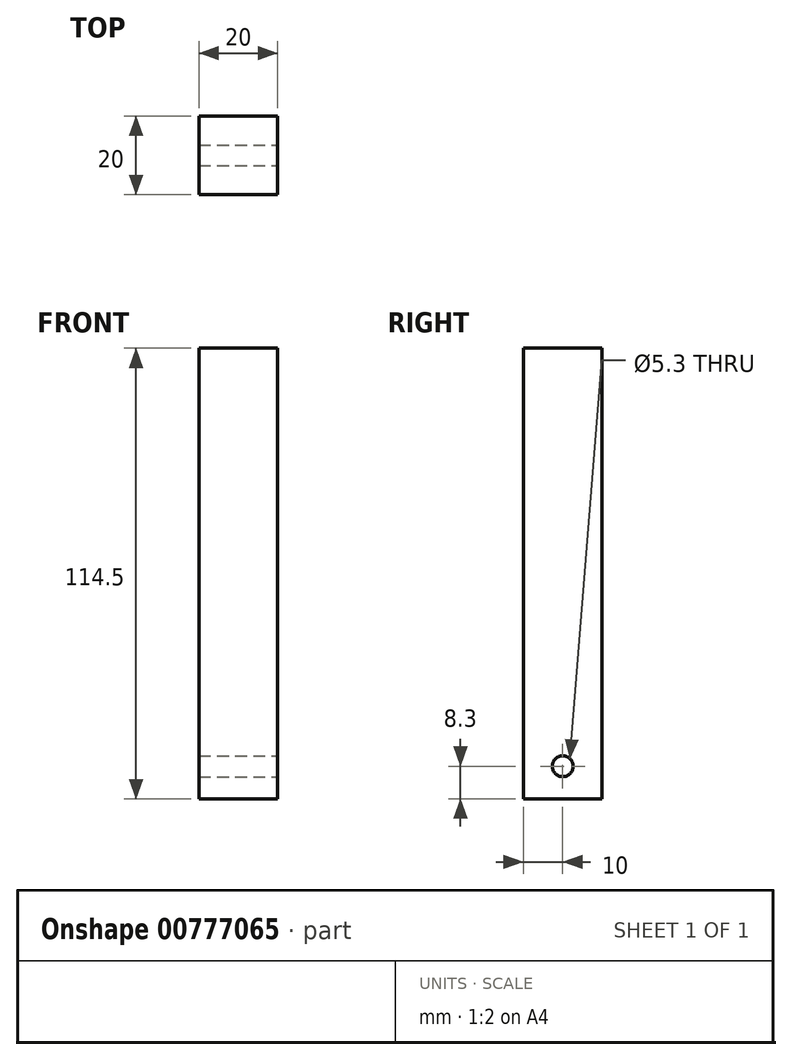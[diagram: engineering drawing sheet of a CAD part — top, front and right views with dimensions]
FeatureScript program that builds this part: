
annotation { "Feature Type Name" : "Feature", "Feature Type Description" : "" }
export const myFeature = defineFeature(function(context is Context, id is Id, definition is map)
    precondition{}
    {
        {
            var Q0;
            Q0=qCreatedBy(makeId("Top.planeOp"),FACE);
            var sketch = newSketch(context, id + "F0", { "sketchPlane" : qUnion([Q0])});
            skLineSegment(sketch, "E0.bottom", {"start": v(-10, 10) * mm, "end": v(10, 10) * mm});
            skLineSegment(sketch, "E0.top", {"start": v(-10, -10) * mm, "end": v(10, -10) * mm});
            skLineSegment(sketch, "E0.left", {"start": v(-10, 10) * mm, "end": v(-10, -10) * mm});
            skLineSegment(sketch, "E0.right", {"start": v(10, 10) * mm, "end": v(10, -10) * mm});
            skSolve(sketch);
        }
        {
            var Q0;
            Q0=qSketchRegion(id+"F0",true);
            extrude(context, id + "F1", {"entities" : qUnion([Q0]), "depth" : (104.5 + 10) * mm, "offsetDistance" : 25 * mm});
        }
        {
            var Q0;
            Q0=makeQuery(id+"F1.opExtrude","SWEPT_FACE",FACE,{"disambiguationData":[OSD([sQuery(id+"F0.wireOp",EDGE,"E0.right")])]});
            var sketch = newSketch(context, id + "F2", { "sketchPlane" : qUnion([Q0])});
            skCircle(sketch, "E1", {"center": v(0, 10) * mm, "radius": 2.5 * mm});
            skSolve(sketch);
        }
        {
            var Q0;
            Q0=makeQuery(id+"F2.imprint","IMPRINT",FACE,{"disambiguationData":[TD([[makeQuery(id+"F2.imprint","IMPRINT",EDGE,{"derivedFrom":sQuery(id+"F2.wireOp",EDGE,"E1")}),-1.0]])]});
            var sketch = newSketch(context, id + "F3", { "sketchPlane" : qUnion([Q0])});
            skCircle(sketch, "E2", {"center": v(0, 8.3) * mm, "radius": 2.65 * mm});
            skSolve(sketch);
        }
        {
            var Q0;
            Q0=qSketchRegion(id+"F3",true);
            extrude(context, id + "F4", {"entities" : qUnion([Q0]), "operationType" : NewBodyOperationType.REMOVE, "endBound" : BoundingType.THROUGH_ALL, "oppositeDirection" : true, "depth" : 25 * mm});
        }
    });
